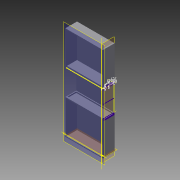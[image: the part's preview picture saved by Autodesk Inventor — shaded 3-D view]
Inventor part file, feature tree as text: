
AUTODESK INVENTOR PART (.ipt)
format: ipt  version: 2015 (Build 190159000, 159)  size: 166,912 bytes
history: native  units: mm
features: sketch x9, extrude x5, projected_geometry x3
ambient origin geometry x8: Origin, YZ Plane, XZ Plane, XY Plane, X Axis, Y Axis, Z Axis, Center Point
bodies: Solid1 (feature_tree)
feature tree (17):
  sketch  "Sketch1"  dims[d0=241.25mm d1=96.5mm]
  sketch  "Sketch2"  dims[d2=30.0mm d3=0.0mm d4=64.0mm]
  extrude  "Extrusion1"  Depth=96.5mm
  extrude  "Extrusion2"  Depth=64.0mm
  extrude  "Extrusion3"  Depth=96.5mm
  sketch  "Sketch6"  dims[d12=28.0mm d13=0.0mm]
  sketch  "Sketch7"  dims[d28=2.0mm]
  sketch  "Sketch9"  dims[d29=4.0mm]
  extrude  "Extrusion5"  Depth=28.0mm TaperAngle=0.0deg
  extrude  "Extrusion6"  Depth=2.0mm
  sketch  "Sketch11"  dims[d30=3.0mm d31=2.0mm d32=2.0mm d33=0.0mm d34=94.5mm d35=0.0mm d36=22.0mm d37=2.0mm d38=5.0mm]
  sketch  "Sketch3"  dims[d5=0.0mm d6=96.5mm]
  sketch  "Sketch4"  dims[d7=0.0mm d8=28.0mm d9=0.0mm]
  sketch  "Sketch5"  dims[d10=2.0mm d11=2.0mm]
  projected_geometry  "Projected Loop1"
  projected_geometry  "Projected Loop2"
  projected_geometry  "Projected Loop3"
